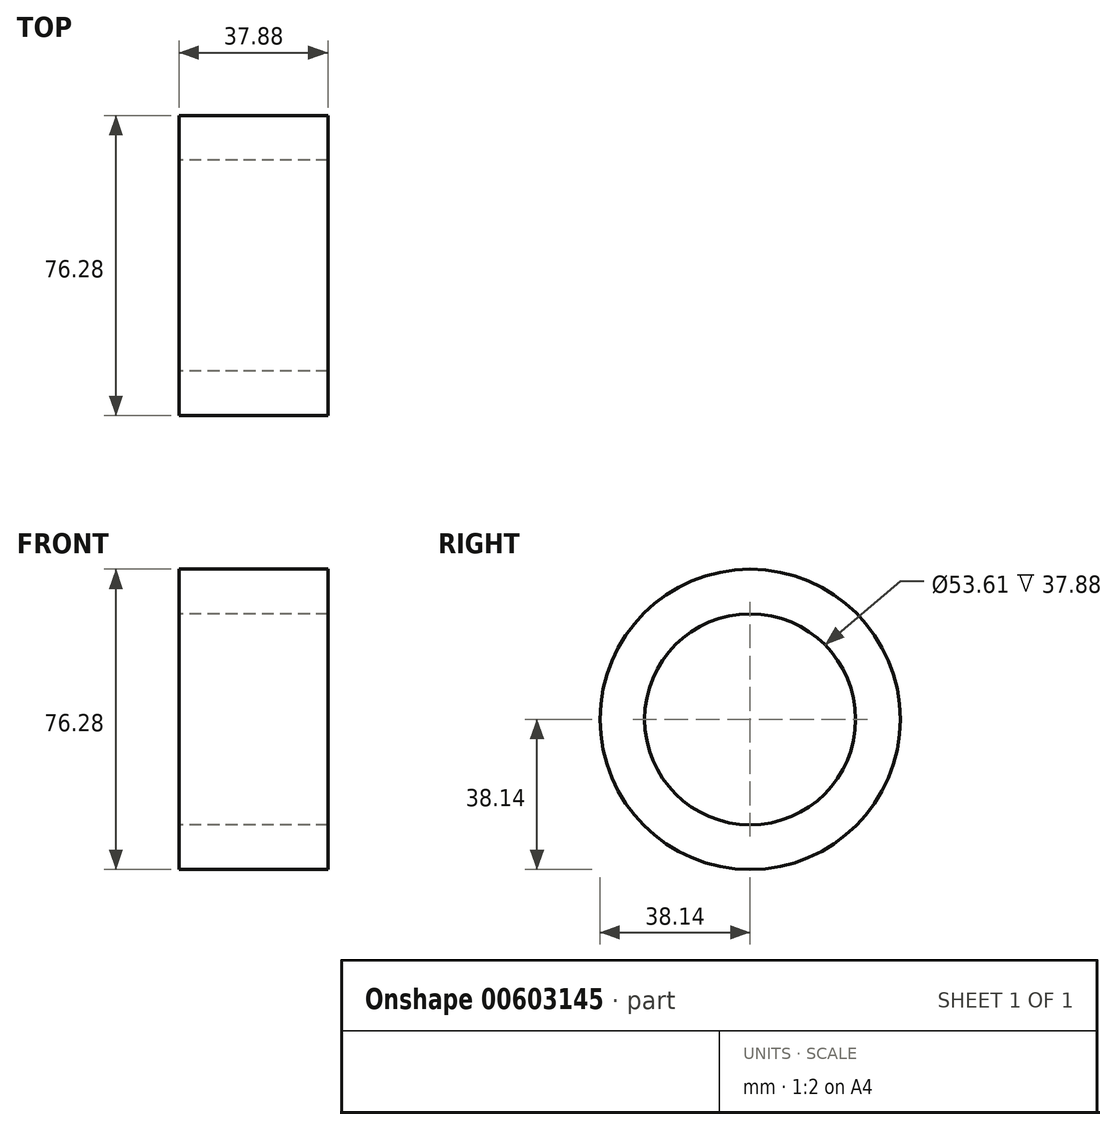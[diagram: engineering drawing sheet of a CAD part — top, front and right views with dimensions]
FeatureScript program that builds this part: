
annotation { "Feature Type Name" : "Feature", "Feature Type Description" : "" }
export const myFeature = defineFeature(function(context is Context, id is Id, definition is map)
    precondition{}
    {
        {
            var Q0;
            Q0=qCreatedBy(makeId("Right.planeOp"),FACE);
            var sketch = newSketch(context, id + "F0", { "sketchPlane" : qUnion([Q0])});
            skCircle(sketch, "E0.cCircle", {"center": v(0, 0) * mm, "radius": 33.65 * mm, "construction": true});
            skLineSegment(sketch, "E0.0", {"start": v(-1.97, 38.8) * mm, "end": v(32.62, 21.11) * mm});
            skLineSegment(sketch, "E0.1", {"start": v(32.62, 21.11) * mm, "end": v(34.6, -17.7) * mm});
            skLineSegment(sketch, "E0.2", {"start": v(34.6, -17.7) * mm, "end": v(1.97, -38.8) * mm});
            skLineSegment(sketch, "E0.3", {"start": v(1.97, -38.8) * mm, "end": v(-32.62, -21.11) * mm});
            skLineSegment(sketch, "E0.4", {"start": v(-32.62, -21.11) * mm, "end": v(-34.6, 17.7) * mm});
            skLineSegment(sketch, "E0.5", {"start": v(-34.6, 17.7) * mm, "end": v(-1.97, 38.8) * mm});
            skPoint(sketch, "E0.0.midPoint", {"position": v(15.33, 29.96) * mm});
            skCircle(sketch, "E1", {"center": v(0, 0) * mm, "radius": 26.8 * mm});
            skCircle(sketch, "E2", {"center": v(0, 0) * mm, "radius": 31.44 * mm});
            skCircle(sketch, "E3", {"center": v(0, 0) * mm, "radius": 38.14 * mm});
            skCircle(sketch, "E4", {"center": v(0, 0) * mm, "radius": 29.05 * mm});
            skSolve(sketch);
        }
        {
            var Q0;
            {var subQ0=sQuery(id+"F0.wireOp",EDGE,"E3");var subQ1=sQuery(id+"F0.wireOp",EDGE,"E0.0");var subQ2=makeQuery(id+"F0.imprint","INTERSECT",VERTEX,{"disambiguationData":[OD(0.0)],"derivedFrom":[subQ1,subQ0]});Q0=makeQuery(id+"F0.imprint","IMPRINT",FACE,{"disambiguationData":[TD([[makeQuery(id+"F0.imprint","IMPRINT",EDGE,{"disambiguationData":[TD([[subQ2,-1.0]])],"derivedFrom":subQ1}),1.0]])]});}
            var Q1;
            {var subQ0=sQuery(id+"F0.wireOp",EDGE,"E3");var subQ1=sQuery(id+"F0.wireOp",EDGE,"E0.5");var subQ2=makeQuery(id+"F0.imprint","INTERSECT",VERTEX,{"disambiguationData":[OD(0.0)],"derivedFrom":[subQ1,subQ0]});Q1=makeQuery(id+"F0.imprint","IMPRINT",FACE,{"disambiguationData":[TD([[makeQuery(id+"F0.imprint","IMPRINT",EDGE,{"disambiguationData":[TD([[subQ2,-1.0]])],"derivedFrom":subQ1}),1.0]])]});}
            var Q2;
            {var subQ0=sQuery(id+"F0.wireOp",EDGE,"E3");var subQ1=sQuery(id+"F0.wireOp",EDGE,"E0.4");var subQ2=makeQuery(id+"F0.imprint","INTERSECT",VERTEX,{"disambiguationData":[OD(0.0)],"derivedFrom":[subQ1,subQ0]});Q2=makeQuery(id+"F0.imprint","IMPRINT",FACE,{"disambiguationData":[TD([[makeQuery(id+"F0.imprint","IMPRINT",EDGE,{"disambiguationData":[TD([[subQ2,-1.0]])],"derivedFrom":subQ1}),1.0]])]});}
            var Q3;
            {var subQ0=sQuery(id+"F0.wireOp",EDGE,"E3");var subQ1=sQuery(id+"F0.wireOp",EDGE,"E0.3");var subQ2=makeQuery(id+"F0.imprint","INTERSECT",VERTEX,{"disambiguationData":[OD(0.0)],"derivedFrom":[subQ1,subQ0]});Q3=makeQuery(id+"F0.imprint","IMPRINT",FACE,{"disambiguationData":[TD([[makeQuery(id+"F0.imprint","IMPRINT",EDGE,{"disambiguationData":[TD([[subQ2,-1.0]])],"derivedFrom":subQ1}),1.0]])]});}
            var Q4;
            {var subQ0=sQuery(id+"F0.wireOp",EDGE,"E3");var subQ1=sQuery(id+"F0.wireOp",EDGE,"E0.2");var subQ2=makeQuery(id+"F0.imprint","INTERSECT",VERTEX,{"disambiguationData":[OD(0.0)],"derivedFrom":[subQ1,subQ0]});Q4=makeQuery(id+"F0.imprint","IMPRINT",FACE,{"disambiguationData":[TD([[makeQuery(id+"F0.imprint","IMPRINT",EDGE,{"disambiguationData":[TD([[subQ2,-1.0]])],"derivedFrom":subQ1}),1.0]])]});}
            var Q5;
            Q5=makeQuery(id+"F0.imprint","IMPRINT",FACE,{"disambiguationData":[TD([[makeQuery(id+"F0.imprint","IMPRINT",EDGE,{"derivedFrom":sQuery(id+"F0.wireOp",EDGE,"E2")}),-1.0]])]});
            var Q6;
            {var subQ0=sQuery(id+"F0.wireOp",EDGE,"E3");var subQ1=sQuery(id+"F0.wireOp",EDGE,"E0.1");var subQ2=makeQuery(id+"F0.imprint","INTERSECT",VERTEX,{"disambiguationData":[OD(0.0)],"derivedFrom":[subQ1,subQ0]});Q6=makeQuery(id+"F0.imprint","IMPRINT",FACE,{"disambiguationData":[TD([[makeQuery(id+"F0.imprint","IMPRINT",EDGE,{"disambiguationData":[TD([[subQ2,-1.0]])],"derivedFrom":subQ1}),1.0]])]});}
            var Q7;
            Q7=makeQuery(id+"F0.imprint","IMPRINT",FACE,{"disambiguationData":[TD([[makeQuery(id+"F0.imprint","IMPRINT",EDGE,{"derivedFrom":sQuery(id+"F0.wireOp",EDGE,"E1")}),-1.0]])]});
            var Q8;
            Q8=makeQuery(id+"F0.imprint","IMPRINT",FACE,{"disambiguationData":[TD([[makeQuery(id+"F0.imprint","IMPRINT",EDGE,{"derivedFrom":sQuery(id+"F0.wireOp",EDGE,"E2")}),1.0]])]});
            var Q9;
            Q9=sQuery(id+"F0.wireOp",EDGE,"E3");
            extrude(context, id + "F1", {"entities" : qUnion([Q0, Q1, Q2, Q3, Q4, Q5, Q6, Q7, Q8]), "surfaceEntities" : qUnion([Q9]), "depth" : 37.88 * mm, "offsetDistance" : 25 * mm});
        }
        {
            var Q0;
            Q0=qCreatedBy(makeId("Right.planeOp"),FACE);
            cPlane(context, id + "F2", {"entities" : qUnion([Q0]), "cplaneType" : CPlaneType.OFFSET, "offset" : 37.88 * mm, "width" : 150 * mm, "height" : 150 * mm});
        }
        {
            var Q0;
            Q0=qCreatedBy(makeId("Front.planeOp"),FACE);
            var sketch = newSketch(context, id + "F3", { "sketchPlane" : qUnion([Q0])});
            skLineSegment(sketch, "E5", {"start": v(37.88, 38.28) * mm, "end": v(28.13, 38.2) * mm});
            skLineSegment(sketch, "E6", {"start": v(37.88, -38.08) * mm, "end": v(28.13, -38.08) * mm});
            skLineSegment(sketch, "E7", {"start": v(28.13, 38.2) * mm, "end": v(28.13, -38.08) * mm});
            skLineSegment(sketch, "E8", {"start": v(13.03, 38.09) * mm, "end": v(13.03, -38.2) * mm});
            skLineSegment(sketch, "E9", {"start": v(31.6, 38.23) * mm, "end": v(31.6, -38.08) * mm});
            skLineSegment(sketch, "E10", {"start": v(0, 0) * mm, "end": v(0, 29.05) * mm});
            skLineSegment(sketch, "E11.MirrorCS", {"start": v(0, 0) * mm, "end": v(0, -29.05) * mm});
            skLineSegment(sketch, "E12", {"start": v(0, 0) * mm, "end": v(0, 31.44) * mm});
            skLineSegment(sketch, "E13", {"start": v(0, -31.44) * mm, "end": v(0, 31.44) * mm});
            skLineSegment(sketch, "E14", {"start": v(0, 31.44) * mm, "end": v(0, 0) * mm});
            skLineSegment(sketch, "E15", {"start": v(0, 31.44) * mm, "end": v(13.03, 31.44) * mm});
            skLineSegment(sketch, "E16", {"start": v(0, -31.44) * mm, "end": v(13.03, -31.44) * mm});
            skLineSegment(sketch, "E17", {"start": v(0, 29.05) * mm, "end": v(13.03, 29.02) * mm});
            skLineSegment(sketch, "E18", {"start": v(0, -29.05) * mm, "end": v(13.03, -29.05) * mm});
            skLineSegment(sketch, "E19", {"start": v(13.03, 29.02) * mm, "end": v(28.1, 29.02) * mm});
            skLineSegment(sketch, "E20", {"start": v(28.13, 29.02) * mm, "end": v(28.1, 29.02) * mm});
            skLineSegment(sketch, "E21", {"start": v(13.03, 31.44) * mm, "end": v(37.88, 31.58) * mm});
            skLineSegment(sketch, "E22", {"start": v(13.03, -31.44) * mm, "end": v(37.88, -31.44) * mm});
            skLineSegment(sketch, "E23.bottom", {"start": v(0, 29.05) * mm, "end": v(13.03, 29.05) * mm});
            skLineSegment(sketch, "E23.left", {"start": v(0, 29.05) * mm, "end": v(0, -29.05) * mm});
            skLineSegment(sketch, "E23.right", {"start": v(13.03, 29.05) * mm, "end": v(13.03, -29.05) * mm});
            skLineSegment(sketch, "E24.bottom", {"start": v(13.03, -29.05) * mm, "end": v(0, -29.05) * mm});
            skLineSegment(sketch, "E24.top", {"start": v(13.03, -29.05) * mm, "end": v(0, -29.05) * mm});
            skLineSegment(sketch, "E24.left", {"start": v(13.03, -29.05) * mm, "end": v(13.03, -29.05) * mm});
            skLineSegment(sketch, "E24.right", {"start": v(0, -29.05) * mm, "end": v(0, -29.05) * mm});
            skLineSegment(sketch, "E25.top", {"start": v(0, 29.02) * mm, "end": v(13.03, 29.02) * mm});
            skLineSegment(sketch, "E25.left", {"start": v(0, 29.02) * mm, "end": v(0, 29.05) * mm});
            skLineSegment(sketch, "E25.right", {"start": v(13.03, 29.02) * mm, "end": v(13.03, 29.05) * mm});
            skLineSegment(sketch, "E26", {"start": v(28.1, 29.02) * mm, "end": v(37.88, 29.02) * mm});
            skLineSegment(sketch, "E27", {"start": v(13.03, -29.05) * mm, "end": v(37.88, -29.05) * mm});
            skLineSegment(sketch, "E28", {"start": v(31.61, -38.08) * mm, "end": v(37.88, -31.44) * mm});
            skLineSegment(sketch, "E29", {"start": v(31.6, 38.23) * mm, "end": v(37.88, 31.58) * mm});
            skLineSegment(sketch, "E30", {"start": v(0, 0) * mm, "end": v(0, 38.14) * mm});
            skSolve(sketch);
        }
        {
            var Q0;
            Q0=makeQuery(id+"F0.imprint","IMPRINT",FACE,{"disambiguationData":[TD([[makeQuery(id+"F0.imprint","IMPRINT",EDGE,{"derivedFrom":sQuery(id+"F0.wireOp",EDGE,"E2")}),-1.0]])]});
            var Q1;
            {var subQ0=sQuery(id+"F0.wireOp",EDGE,"E3");var subQ1=sQuery(id+"F0.wireOp",EDGE,"E0.0");var subQ2=makeQuery(id+"F0.imprint","INTERSECT",VERTEX,{"disambiguationData":[OD(0.0)],"derivedFrom":[subQ1,subQ0]});Q1=makeQuery(id+"F0.imprint","IMPRINT",FACE,{"disambiguationData":[TD([[makeQuery(id+"F0.imprint","IMPRINT",EDGE,{"disambiguationData":[TD([[subQ2,-1.0]])],"derivedFrom":subQ1}),1.0]])]});}
            var Q2;
            {var subQ0=sQuery(id+"F0.wireOp",EDGE,"E3");var subQ1=sQuery(id+"F0.wireOp",EDGE,"E0.5");var subQ2=makeQuery(id+"F0.imprint","INTERSECT",VERTEX,{"disambiguationData":[OD(0.0)],"derivedFrom":[subQ1,subQ0]});Q2=makeQuery(id+"F0.imprint","IMPRINT",FACE,{"disambiguationData":[TD([[makeQuery(id+"F0.imprint","IMPRINT",EDGE,{"disambiguationData":[TD([[subQ2,-1.0]])],"derivedFrom":subQ1}),1.0]])]});}
            var Q3;
            {var subQ0=sQuery(id+"F0.wireOp",EDGE,"E3");var subQ1=sQuery(id+"F0.wireOp",EDGE,"E0.4");var subQ2=makeQuery(id+"F0.imprint","INTERSECT",VERTEX,{"disambiguationData":[OD(0.0)],"derivedFrom":[subQ1,subQ0]});Q3=makeQuery(id+"F0.imprint","IMPRINT",FACE,{"disambiguationData":[TD([[makeQuery(id+"F0.imprint","IMPRINT",EDGE,{"disambiguationData":[TD([[subQ2,-1.0]])],"derivedFrom":subQ1}),1.0]])]});}
            var Q4;
            {var subQ0=sQuery(id+"F0.wireOp",EDGE,"E3");var subQ1=sQuery(id+"F0.wireOp",EDGE,"E0.3");var subQ2=makeQuery(id+"F0.imprint","INTERSECT",VERTEX,{"disambiguationData":[OD(0.0)],"derivedFrom":[subQ1,subQ0]});Q4=makeQuery(id+"F0.imprint","IMPRINT",FACE,{"disambiguationData":[TD([[makeQuery(id+"F0.imprint","IMPRINT",EDGE,{"disambiguationData":[TD([[subQ2,-1.0]])],"derivedFrom":subQ1}),1.0]])]});}
            var Q5;
            {var subQ0=sQuery(id+"F0.wireOp",EDGE,"E3");var subQ1=sQuery(id+"F0.wireOp",EDGE,"E0.2");var subQ2=makeQuery(id+"F0.imprint","INTERSECT",VERTEX,{"disambiguationData":[OD(0.0)],"derivedFrom":[subQ1,subQ0]});Q5=makeQuery(id+"F0.imprint","IMPRINT",FACE,{"disambiguationData":[TD([[makeQuery(id+"F0.imprint","IMPRINT",EDGE,{"disambiguationData":[TD([[subQ2,-1.0]])],"derivedFrom":subQ1}),1.0]])]});}
            var Q6;
            {var subQ0=sQuery(id+"F0.wireOp",EDGE,"E3");var subQ1=sQuery(id+"F0.wireOp",EDGE,"E0.1");var subQ2=makeQuery(id+"F0.imprint","INTERSECT",VERTEX,{"disambiguationData":[OD(0.0)],"derivedFrom":[subQ1,subQ0]});Q6=makeQuery(id+"F0.imprint","IMPRINT",FACE,{"disambiguationData":[TD([[makeQuery(id+"F0.imprint","IMPRINT",EDGE,{"disambiguationData":[TD([[subQ2,-1.0]])],"derivedFrom":subQ1}),1.0]])]});}
            extrude(context, id + "F4", {"entities" : qUnion([Q0, Q1, Q2, Q3, Q4, Q5, Q6]), "operationType" : NewBodyOperationType.REMOVE, "oppositeDirection" : true, "depth" : 28.13 * mm, "offsetDistance" : 25 * mm});
        }
        {
            var Q0;
            Q0=qCreatedBy(makeId("Right.planeOp"),FACE);
            var Q1;
            Q1=sQuery(id+"F3.wireOp",VERTEX,"E7.start");
            cPlane(context, id + "F5", {"entities" : qUnion([Q0, Q1]), "cplaneType" : CPlaneType.PLANE_POINT, "offset" : 0 * mm, "width" : 150 * mm, "height" : 150 * mm});
        }
    });
